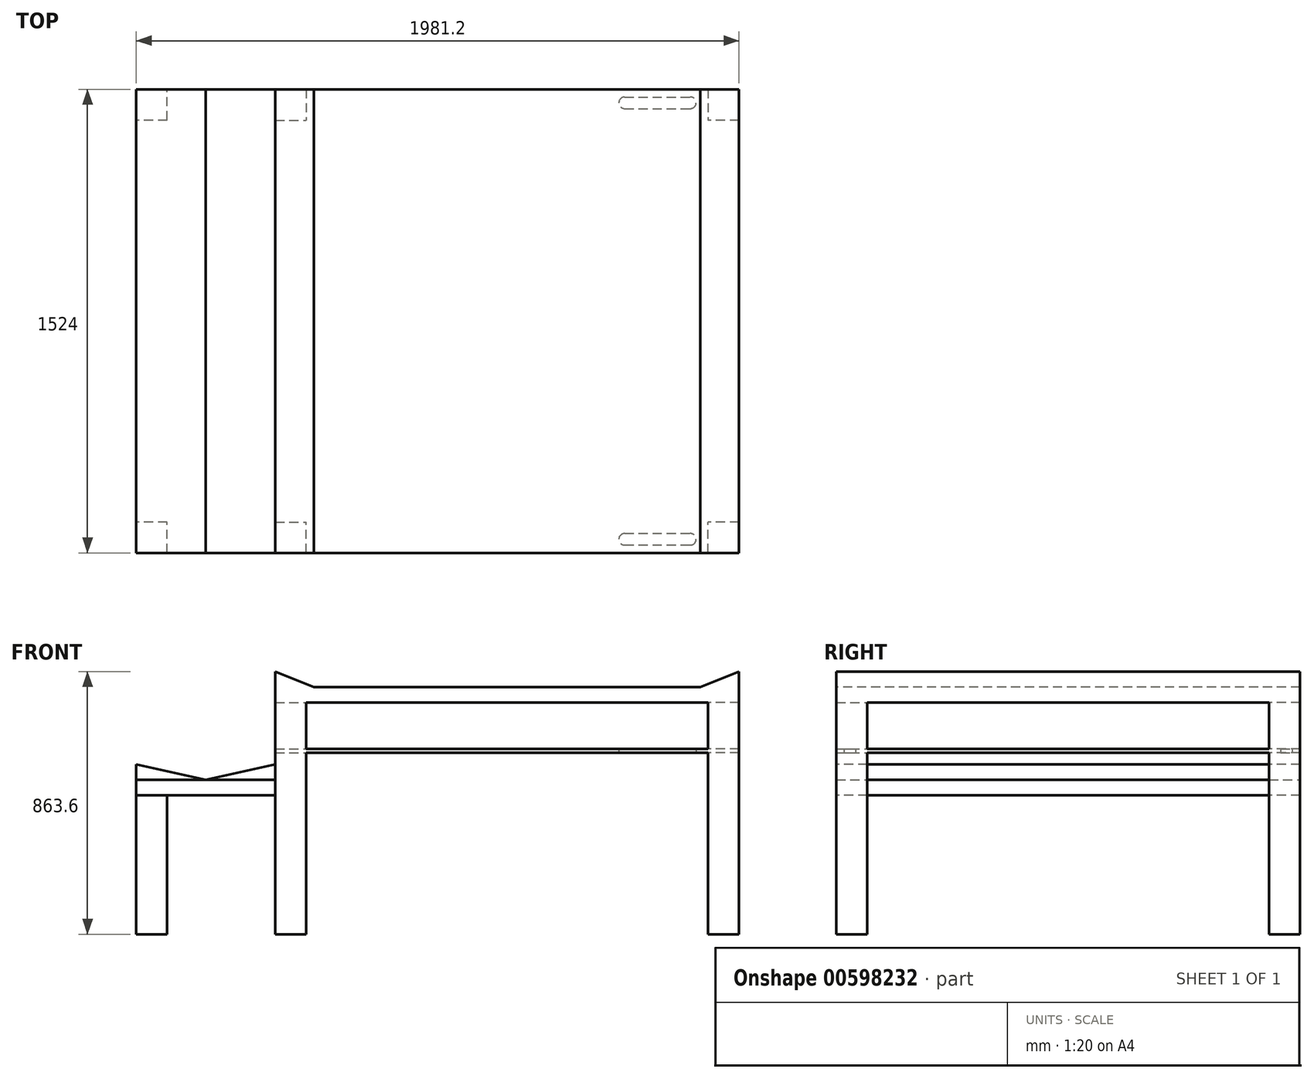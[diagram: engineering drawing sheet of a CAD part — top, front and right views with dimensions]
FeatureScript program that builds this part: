
annotation { "Feature Type Name" : "Feature", "Feature Type Description" : "" }
export const myFeature = defineFeature(function(context is Context, id is Id, definition is map)
    precondition{}
    {
        {
            var Q0;
            Q0=qCreatedBy(makeId("Top.planeOp"),FACE);
            var sketch = newSketch(context, id + "F0", { "sketchPlane" : qUnion([Q0])});
            skLineSegment(sketch, "E0.bottom", {"start": v(0, 0) * mm, "end": v(1524, 0) * mm});
            skLineSegment(sketch, "E0.top", {"start": v(0, 1524) * mm, "end": v(1524, 1524) * mm});
            skLineSegment(sketch, "E0.left", {"start": v(0, 0) * mm, "end": v(0, 1524) * mm});
            skLineSegment(sketch, "E0.right", {"start": v(1524, 0) * mm, "end": v(1524, 1524) * mm});
            skSolve(sketch);
        }
        {
            var Q0;
            Q0 = qSketchRegion(id + "F0", true);
            extrude(context, id + "F1", {"entities" : qUnion([Q0]), "depth" : 50.8 * mm, "offsetDistance" : 25.4 * mm});
        }
        {
            var Q0;
            Q0=makeQuery(id+"F1.opExtrude","CAP_FACE",FACE,{"disambiguationData":[OSD([sQuery(id+"F0.wireOp",EDGE,"E0.bottom"),sQuery(id+"F0.wireOp",EDGE,"E0.top"),sQuery(id+"F0.wireOp",EDGE,"E0.left"),sQuery(id+"F0.wireOp",EDGE,"E0.right")])],"isStart":true});
            var sketch = newSketch(context, id + "F2", { "sketchPlane" : qUnion([Q0])});
            skLineSegment(sketch, "E1.bottom", {"start": v(0, 0) * mm, "end": v(101.6, 0) * mm});
            skLineSegment(sketch, "E1.top", {"start": v(0, -101.6) * mm, "end": v(101.6, -101.6) * mm});
            skLineSegment(sketch, "E1.left", {"start": v(0, 0) * mm, "end": v(0, -101.6) * mm});
            skLineSegment(sketch, "E1.right", {"start": v(101.6, 0) * mm, "end": v(101.6, -101.6) * mm});
            skLineSegment(sketch, "E2.bottom", {"start": v(1524, 0) * mm, "end": v(1422.4, 0) * mm});
            skLineSegment(sketch, "E2.top", {"start": v(1524, -101.6) * mm, "end": v(1422.4, -101.6) * mm});
            skLineSegment(sketch, "E2.left", {"start": v(1524, 0) * mm, "end": v(1524, -101.6) * mm});
            skLineSegment(sketch, "E2.right", {"start": v(1422.4, 0) * mm, "end": v(1422.4, -101.6) * mm});
            skLineSegment(sketch, "E3.bottom", {"start": v(1524, -1524) * mm, "end": v(1422.4, -1524) * mm});
            skLineSegment(sketch, "E3.top", {"start": v(1524, -1422.4) * mm, "end": v(1422.4, -1422.4) * mm});
            skLineSegment(sketch, "E3.left", {"start": v(1524, -1524) * mm, "end": v(1524, -1422.4) * mm});
            skLineSegment(sketch, "E3.right", {"start": v(1422.4, -1524) * mm, "end": v(1422.4, -1422.4) * mm});
            skLineSegment(sketch, "E4.bottom", {"start": v(0, -1524) * mm, "end": v(101.6, -1524) * mm});
            skLineSegment(sketch, "E4.top", {"start": v(0, -1422.4) * mm, "end": v(101.6, -1422.4) * mm});
            skLineSegment(sketch, "E4.left", {"start": v(0, -1524) * mm, "end": v(0, -1422.4) * mm});
            skLineSegment(sketch, "E4.right", {"start": v(101.6, -1524) * mm, "end": v(101.6, -1422.4) * mm});
            skSolve(sketch);
        }
        {
            var Q0;
            Q0 = qSketchRegion(id + "F2", true);
            extrude(context, id + "F3", {"entities" : qUnion([Q0]), "operationType" : NewBodyOperationType.ADD, "depth" : 762 * mm, "offsetDistance" : 25.4 * mm});
        }
        {
            var Q0;
            Q0=qCreatedBy(makeId("Front.planeOp"),FACE);
            var sketch = newSketch(context, id + "F4", { "sketchPlane" : qUnion([Q0])});
            skLineSegment(sketch, "E5", {"start": v(0, 0) * mm, "end": v(0, -152.4) * mm});
            skLineSegment(sketch, "E6", {"start": v(0, -152.4) * mm, "end": v(1524, -152.4) * mm});
            skLineSegment(sketch, "E7", {"start": v(0, -152.4) * mm, "end": v(0, -165.1) * mm});
            skLineSegment(sketch, "E8", {"start": v(0, -165.1) * mm, "end": v(1524, -165.1) * mm});
            skLineSegment(sketch, "E9", {"start": v(1524, -165.1) * mm, "end": v(1524, -152.4) * mm});
            skSolve(sketch);
        }
        {
            var Q0;
            Q0 = qSketchRegion(id + "F4", true);
            extrude(context, id + "F5", {"entities" : qUnion([Q0]), "operationType" : NewBodyOperationType.ADD, "oppositeDirection" : true, "depth" : 1524 * mm, "offsetDistance" : 25.4 * mm});
        }
        {
            var Q0;
            Q0=makeQuery(id+"F5.opExtrude","SWEPT_FACE",FACE,{"disambiguationData":[OSD([sQuery(id+"F4.wireOp",EDGE,"E8")])]});
            var sketch = newSketch(context, id + "F6", { "sketchPlane" : qUnion([Q0])});
            skLineSegment(sketch, "E10.bottom", {"start": v(1148.06, -25.6) * mm, "end": v(1363.96, -25.6) * mm});
            skLineSegment(sketch, "E10.top", {"start": v(1148.06, -63.7) * mm, "end": v(1363.96, -63.7) * mm});
            skLineSegment(sketch, "E10.left", {"start": v(1129.01, -44.65) * mm, "end": v(1129.01, -44.65) * mm});
            skLineSegment(sketch, "E10.right", {"start": v(1383.01, -44.65) * mm, "end": v(1383.01, -44.65) * mm});
            skPoint(sketch, "E11.visualSharp", {"position": v(1129.01, -25.6) * mm});
            skArc(sketch, "E11.filletArc", {"start": v(1148.06, -25.6) * mm, "mid": v(1134.6, -31.18) * mm, "end": v(1129.01, -44.65) * mm});
            skPoint(sketch, "E12.visualSharp", {"position": v(1129.01, -63.7) * mm});
            skArc(sketch, "E12.filletArc", {"start": v(1129.01, -44.65) * mm, "mid": v(1134.6, -58.12) * mm, "end": v(1148.06, -63.7) * mm});
            skPoint(sketch, "E13.visualSharp", {"position": v(1383.01, -25.6) * mm});
            skArc(sketch, "E13.filletArc", {"start": v(1383.01, -44.65) * mm, "mid": v(1377.44, -31.18) * mm, "end": v(1363.96, -25.6) * mm});
            skPoint(sketch, "E14.visualSharp", {"position": v(1383.01, -63.7) * mm});
            skArc(sketch, "E14.filletArc", {"start": v(1363.96, -63.7) * mm, "mid": v(1377.44, -58.12) * mm, "end": v(1383.01, -44.65) * mm});
            skLineSegment(sketch, "E15", {"start": v(0, -762) * mm, "end": v(1524, -762) * mm});
            skLineSegment(sketch, "E16.MirrorCS", {"start": v(1148.06, -1460.3) * mm, "end": v(1363.96, -1460.3) * mm});
            skArc(sketch, "E17.MirrorCS", {"start": v(1363.96, -1460.3) * mm, "mid": v(1377.44, -1465.88) * mm, "end": v(1383.01, -1479.35) * mm});
            skArc(sketch, "E18.MirrorCS", {"start": v(1383.01, -1479.35) * mm, "mid": v(1377.44, -1492.82) * mm, "end": v(1363.96, -1498.4) * mm});
            skLineSegment(sketch, "E19.MirrorCS", {"start": v(1148.06, -1498.4) * mm, "end": v(1363.96, -1498.4) * mm});
            skArc(sketch, "E20.MirrorCS", {"start": v(1148.06, -1498.4) * mm, "mid": v(1134.6, -1492.82) * mm, "end": v(1129.01, -1479.35) * mm});
            skArc(sketch, "E21.MirrorCS", {"start": v(1129.01, -1479.35) * mm, "mid": v(1134.6, -1465.88) * mm, "end": v(1148.06, -1460.3) * mm});
            skSolve(sketch);
        }
        {
            var Q0;
            Q0 = qSketchRegion(id + "F6", true);
            extrude(context, id + "F7", {"entities" : qUnion([Q0]), "operationType" : NewBodyOperationType.REMOVE, "oppositeDirection" : true, "depth" : 25.4 * mm, "offsetDistance" : 25.4 * mm});
        }
        {
            var Q0;
            Q0=qCreatedBy(makeId("Front.planeOp"),FACE);
            var sketch = newSketch(context, id + "F8", { "sketchPlane" : qUnion([Q0])});
            skLineSegment(sketch, "E22", {"start": v(0, 50.8) * mm, "end": v(0, 101.6) * mm});
            skLineSegment(sketch, "E23", {"start": v(0, 50.8) * mm, "end": v(127, 50.8) * mm});
            skLineSegment(sketch, "E24", {"start": v(127, 50.8) * mm, "end": v(0, 101.6) * mm});
            skLineSegment(sketch, "E25", {"start": v(762, 0) * mm, "end": v(762, 50.8) * mm});
            skLineSegment(sketch, "E26.MirrorCS", {"start": v(1397, 50.8) * mm, "end": v(1524, 101.6) * mm});
            skLineSegment(sketch, "E27.MirrorCS", {"start": v(1524, 50.8) * mm, "end": v(1524, 101.6) * mm});
            skLineSegment(sketch, "E28.MirrorCS", {"start": v(1524, 50.8) * mm, "end": v(1397, 50.8) * mm});
            skSolve(sketch);
        }
        {
            var Q0;
            Q0 = qSketchRegion(id + "F8", true);
            extrude(context, id + "F9", {"entities" : qUnion([Q0]), "operationType" : NewBodyOperationType.ADD, "oppositeDirection" : true, "depth" : 1524 * mm, "offsetDistance" : 25.4 * mm});
        }
        {
            var Q0;
            Q0=makeQuery(id+"F9.boolean.opBoolean","MERGE",FACE,{"derivedFrom":[makeQuery(id+"F5.boolean.opBoolean","MERGE",FACE,{"derivedFrom":[makeQuery(id+"F3.boolean.opBoolean","MERGE",FACE,{"derivedFrom":[makeQuery(id+"F1.opExtrude","SWEPT_FACE",FACE,{"disambiguationData":[OSD([sQuery(id+"F0.wireOp",EDGE,"E0.left")])]}),makeQuery(id+"F3.opExtrude","SWEPT_FACE",FACE,{"disambiguationData":[OSD([sQuery(id+"F2.wireOp",EDGE,"E1.left")])]}),makeQuery(id+"F3.opExtrude","SWEPT_FACE",FACE,{"disambiguationData":[OSD([sQuery(id+"F2.wireOp",EDGE,"E4.left")])]})]}),makeQuery(id+"F5.opExtrude","SWEPT_FACE",FACE,{"disambiguationData":[OSD([sQuery(id+"F4.wireOp",EDGE,"E7")])]})]}),makeQuery(id+"F9.opExtrude","SWEPT_FACE",FACE,{"disambiguationData":[OSD([sQuery(id+"F8.wireOp",EDGE,"E22")])]})]});
            cPlane(context, id + "F10", {"entities" : qUnion([Q0]), "cplaneType" : CPlaneType.OFFSET, "offset" : 457.2 * mm, "width" : 152.4 * mm, "height" : 152.4 * mm});
        }
        {
            var Q0;
            Q0=qCreatedBy(id+"F10.planeOp",FACE);
            var sketch = newSketch(context, id + "F11", { "sketchPlane" : qUnion([Q0])});
            skLineSegment(sketch, "E29", {"start": v(0, -762) * mm, "end": v(-101.6, -762) * mm});
            skLineSegment(sketch, "E30", {"start": v(-101.6, -762) * mm, "end": v(-101.6, -304.8) * mm});
            skLineSegment(sketch, "E31", {"start": v(-101.6, -304.8) * mm, "end": v(0, -304.8) * mm});
            skLineSegment(sketch, "E32", {"start": v(0, -304.8) * mm, "end": v(0, -762) * mm});
            skLineSegment(sketch, "E33", {"start": v(-1422.4, -762) * mm, "end": v(-1524, -762) * mm});
            skLineSegment(sketch, "E34", {"start": v(-1524, -762) * mm, "end": v(-1524, -304.8) * mm});
            skLineSegment(sketch, "E35", {"start": v(-1524, -304.8) * mm, "end": v(-1422.4, -304.8) * mm});
            skLineSegment(sketch, "E36", {"start": v(-1422.4, -304.8) * mm, "end": v(-1422.4, -762) * mm});
            skSolve(sketch);
        }
        {
            var Q0;
            Q0 = qSketchRegion(id + "F11", true);
            extrude(context, id + "F12", {"entities" : qUnion([Q0]), "oppositeDirection" : true, "depth" : 101.6 * mm, "offsetDistance" : 25.4 * mm});
        }
        {
            var Q0;
            Q0=qCreatedBy(id+"F10.planeOp",FACE);
            var sketch = newSketch(context, id + "F13", { "sketchPlane" : qUnion([Q0])});
            skLineSegment(sketch, "E37", {"start": v(0, 0) * mm, "end": v(0, -254) * mm});
            skLineSegment(sketch, "E38", {"start": v(0, -254) * mm, "end": v(-1524, -254) * mm});
            skLineSegment(sketch, "E39", {"start": v(-1524, -254) * mm, "end": v(-1524, -304.8) * mm});
            skLineSegment(sketch, "E40", {"start": v(-1524, -304.8) * mm, "end": v(0, -304.8) * mm});
            skLineSegment(sketch, "E41", {"start": v(0, -304.8) * mm, "end": v(0, -254) * mm});
            skSolve(sketch);
        }
        {
            var Q0;
            Q0 = qSketchRegion(id + "F13", true);
            extrude(context, id + "F14", {"entities" : qUnion([Q0]), "oppositeDirection" : true, "depth" : 457.2 * mm, "offsetDistance" : 25.4 * mm});
        }
        {
            var Q0;
            Q0=makeQuery(id+"F14.opExtrude","SWEPT_FACE",FACE,{"disambiguationData":[OSD([sQuery(id+"F13.wireOp",EDGE,"E41")])]});
            var sketch = newSketch(context, id + "F15", { "sketchPlane" : qUnion([Q0])});
            skLineSegment(sketch, "E42", {"start": v(-457.2, -254) * mm, "end": v(-457.2, -203.2) * mm});
            skLineSegment(sketch, "E43", {"start": v(-457.2, -254) * mm, "end": v(-228.6, -254) * mm});
            skLineSegment(sketch, "E44", {"start": v(-228.6, -254) * mm, "end": v(0, -254) * mm});
            skLineSegment(sketch, "E45", {"start": v(0, -254) * mm, "end": v(0, -203.2) * mm});
            skLineSegment(sketch, "E46", {"start": v(0, -203.2) * mm, "end": v(-228.6, -254) * mm});
            skLineSegment(sketch, "E47", {"start": v(-228.6, -254) * mm, "end": v(-457.2, -203.2) * mm});
            skSolve(sketch);
        }
        {
            var Q0;
            Q0 = qSketchRegion(id + "F15", true);
            extrude(context, id + "F16", {"entities" : qUnion([Q0]), "oppositeDirection" : true, "depth" : 1524 * mm, "offsetDistance" : 25.4 * mm});
        }
    });
